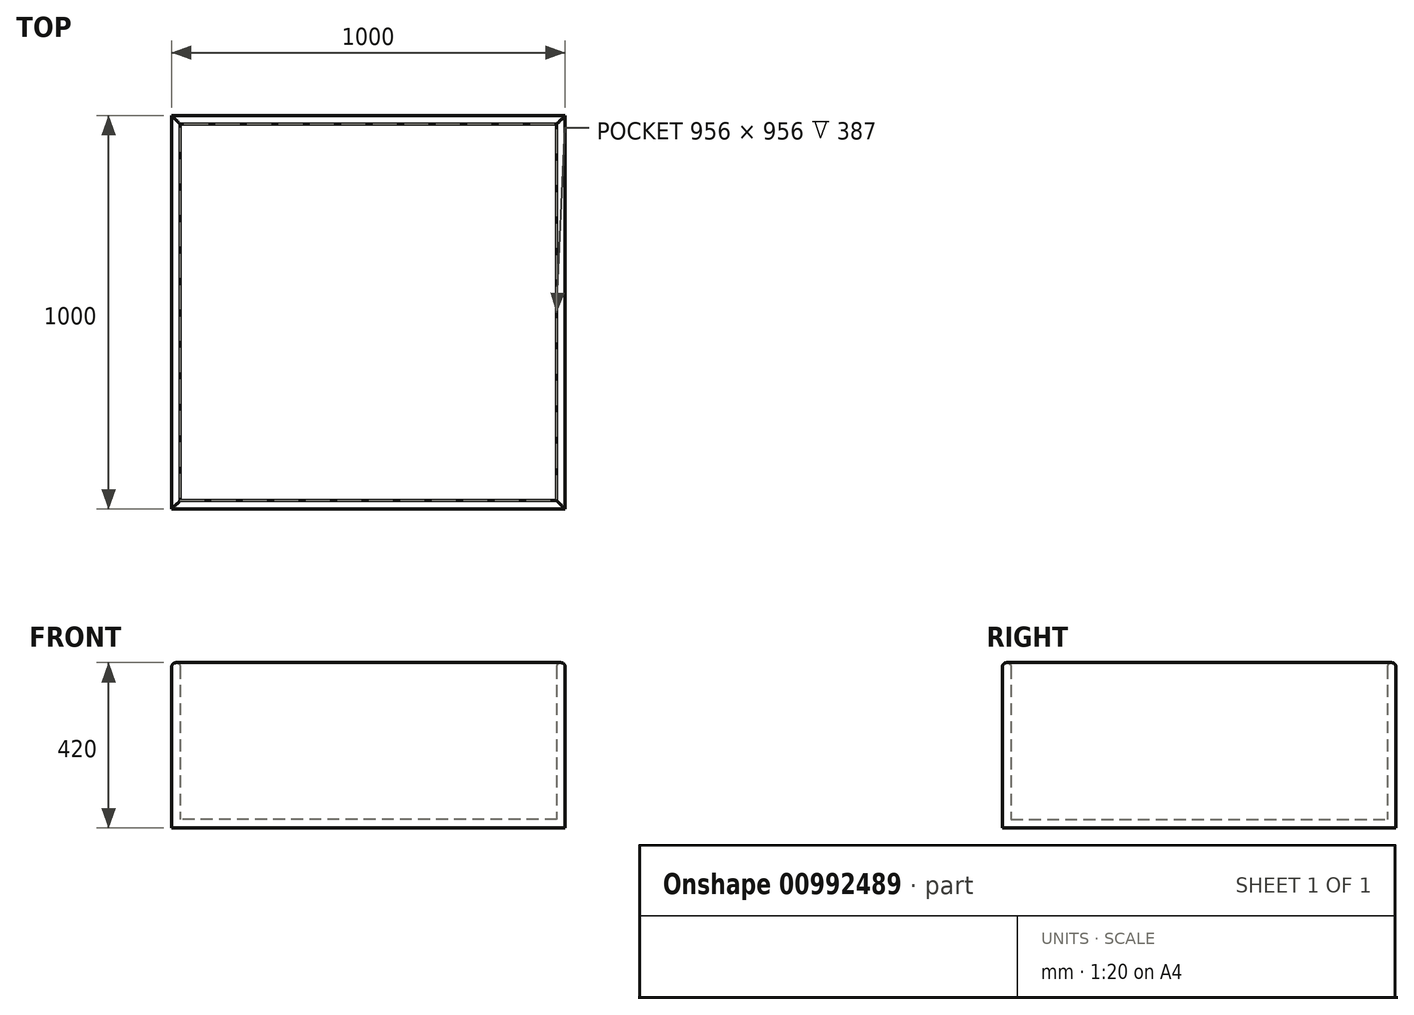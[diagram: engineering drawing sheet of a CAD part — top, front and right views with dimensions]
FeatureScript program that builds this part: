
annotation { "Feature Type Name" : "Feature", "Feature Type Description" : "" }
export const myFeature = defineFeature(function(context is Context, id is Id, definition is map)
    precondition{}
    {
        {
            var Q0;
            Q0=qCreatedBy(makeId("Top.planeOp"),FACE);
            var sketch = newSketch(context, id + "F0", { "sketchPlane" : qUnion([Q0])});
            skLineSegment(sketch, "E0.bottom", {"start": v(500, -500) * mm, "end": v(-500, -500) * mm});
            skLineSegment(sketch, "E0.top", {"start": v(500, 500) * mm, "end": v(-500, 500) * mm});
            skLineSegment(sketch, "E0.left", {"start": v(500, -500) * mm, "end": v(500, 500) * mm});
            skLineSegment(sketch, "E0.right", {"start": v(-500, -500) * mm, "end": v(-500, 500) * mm});
            skPoint(sketch, "E0.middle", {"position": v(0, 0) * mm});
            skLineSegment(sketch, "E1.bottom", {"start": v(188.03, 500) * mm, "end": v(286.32, 500) * mm});
            skLineSegment(sketch, "E1.top", {"start": v(188.03, 500) * mm, "end": v(286.32, 500) * mm});
            skLineSegment(sketch, "E1.left", {"start": v(188.03, 500) * mm, "end": v(188.03, 500) * mm});
            skLineSegment(sketch, "E1.right", {"start": v(286.32, 500) * mm, "end": v(286.32, 500) * mm});
            skPoint(sketch, "E1.middle", {"position": v(237.18, 500) * mm});
            skSolve(sketch);
        }
        {
            var Q0;
            Q0 = qSketchRegion(id + "F0", true);
            extrude(context, id + "F1", {"entities" : qUnion([Q0]), "depth" : 420 * mm, "offsetDistance" : 25 * mm});
        }
        {
            var Q0;
            Q0=makeQuery(id+"F1.opExtrude","CAP_FACE",FACE,{"disambiguationData":[OSD([sQuery(id+"F0.wireOp",EDGE,"E0.bottom"),sQuery(id+"F0.wireOp",EDGE,"E0.top"),sQuery(id+"F0.wireOp",EDGE,"E0.left"),sQuery(id+"F0.wireOp",EDGE,"E0.right"),sQuery(id+"F0.wireOp",EDGE,"E1.top")])],"isStart":false});
            shell(context, id + "F2", {"entities" : qUnion([Q0]), "thickness" : 22 * mm});
        }
        {
            var Q0;
            {var subQ0=sQuery(id+"F0.wireOp",EDGE,"E0.right");Q0=makeQuery(id+"F2.opShell","OFFSET_EDGE",EDGE,{"disambiguationData":[OSD([subQ0]),TDD([makeQuery(id+"F1.opExtrude","CAP_EDGE",EDGE,{"disambiguationData":[OSD([subQ0])],"isStart":false})])]});}
            var Q1;
            {var subQ0=sQuery(id+"F0.wireOp",EDGE,"E1.top");var subQ1=sQuery(id+"F0.wireOp",EDGE,"E0.top");Q1=makeQuery(id+"F2.opShell","OFFSET_EDGE",EDGE,{"disambiguationData":[OSD([subQ1,subQ0]),TDD([makeQuery(id+"F1.opExtrude","CAP_EDGE",EDGE,{"disambiguationData":[OSD([subQ1,subQ0])],"isStart":false})])]});}
            var Q2;
            Q2=makeQuery(id+"F1.opExtrude","CAP_EDGE",EDGE,{"disambiguationData":[OSD([sQuery(id+"F0.wireOp",EDGE,"E0.top"),sQuery(id+"F0.wireOp",EDGE,"E1.top")])],"isStart":false});
            var Q3;
            Q3=makeQuery(id+"F1.opExtrude","CAP_EDGE",EDGE,{"disambiguationData":[OSD([sQuery(id+"F0.wireOp",EDGE,"E0.right")])],"isStart":false});
            var Q4;
            {var subQ0=sQuery(id+"F0.wireOp",EDGE,"E0.bottom");Q4=makeQuery(id+"F2.opShell","OFFSET_EDGE",EDGE,{"disambiguationData":[OSD([subQ0]),TDD([makeQuery(id+"F1.opExtrude","CAP_EDGE",EDGE,{"disambiguationData":[OSD([subQ0])],"isStart":false})])]});}
            var Q5;
            Q5=makeQuery(id+"F1.opExtrude","CAP_EDGE",EDGE,{"disambiguationData":[OSD([sQuery(id+"F0.wireOp",EDGE,"E0.bottom")])],"isStart":false});
            var Q6;
            Q6=makeQuery(id+"F1.opExtrude","CAP_EDGE",EDGE,{"disambiguationData":[OSD([sQuery(id+"F0.wireOp",EDGE,"E0.left")])],"isStart":false});
            var Q7;
            {var subQ0=sQuery(id+"F0.wireOp",EDGE,"E0.left");Q7=makeQuery(id+"F2.opShell","OFFSET_EDGE",EDGE,{"disambiguationData":[OSD([subQ0]),TDD([makeQuery(id+"F1.opExtrude","CAP_EDGE",EDGE,{"disambiguationData":[OSD([subQ0])],"isStart":false})])]});}
            fillet(context, id + "F3", {"entities" : qUnion([Q0, Q1, Q2, Q3, Q4, Q5, Q6, Q7]), "radius" : 11 * mm, "tangentPropagation" : true, "allowEdgeOverflow" : false});
        }
    });
